FCSTD DOCUMENT  (FreeCAD 0.16R6703 (Git))
Label: icestick-case
License: All rights reserved
LicenseURL: http://en.wikipedia.org/wiki/All_rights_reserved
objects: Part::Feature×17, Part::Extrusion×17, Sketcher::SketchObject×10, Part::FeaturePython×10, Part::MultiFuse×7, PartDesign::Pocket×6, Part::Mirroring×6, App::DocumentObjectGroup×6, PartDesign::Pad×4, Part::Cut×2, Part::Part2DObjectPython×1
note: 90 computed .brp shape members not serialized (recipe doc carries the construction recipe); baked Part::Feature solids carry a one-line shape summary decoded from their .brp

FEATURE [Sketcher::SketchObject] Sketch001
  sketch-geometry (12):
    g0: LineSegment StartX=-53 StartY=-13.5 StartZ=0 EndX=-53 EndY=13.5 EndZ=0
    g1: LineSegment StartX=-49 StartY=-17.5 StartZ=0 EndX=49 EndY=-17.5 EndZ=0
    g2: LineSegment StartX=53 StartY=-13.5 StartZ=0 EndX=53 EndY=13.5 EndZ=0
    g3: LineSegment StartX=49 StartY=17.5 StartZ=0 EndX=-49 EndY=17.5 EndZ=0
    g4: ArcOfCircle CenterX=49 CenterY=-13.5 CenterZ=0 NormalX=0 NormalY=0 NormalZ=1 Radius=4 StartAngle=4.71239 EndAngle=6.28319
    g5: ArcOfCircle CenterX=49 CenterY=13.5 CenterZ=0 NormalX=0 NormalY=0 NormalZ=1 Radius=4 StartAngle=0 EndAngle=1.5708
    g6: ArcOfCircle CenterX=-49 CenterY=13.5 CenterZ=0 NormalX=0 NormalY=0 NormalZ=1 Radius=4 StartAngle=1.5708 EndAngle=3.14159
    g7: ArcOfCircle CenterX=-49 CenterY=-13.5 CenterZ=0 NormalX=0 NormalY=0 NormalZ=1 Radius=4 StartAngle=3.14159 EndAngle=4.71239
    g8: LineSegment [constr] StartX=-49 StartY=13.5 StartZ=0 EndX=49 EndY=13.5 EndZ=0
    g9: LineSegment [constr] StartX=49 StartY=13.5 StartZ=0 EndX=49 EndY=-13.5 EndZ=0
    g10: LineSegment [constr] StartX=49 StartY=-13.5 StartZ=0 EndX=-49 EndY=-13.5 EndZ=0
    g11: LineSegment [constr] StartX=-49 StartY=-13.5 StartZ=0 EndX=-49 EndY=13.5 EndZ=0
  constraints (30):
    c: Vertical(g0)
    c: Horizontal(g1)
    c: Vertical(g2)
    c: Horizontal(g3)
    c: Tangent(g1,g4) = -1.5708
    c: Tangent(g2,g4) = -1.5708
    c: Tangent(g2,g5) = -1.5708
    c: Tangent(g3,g5) = -1.5708
    c: Tangent(g0,g6) = 1.5708
    c: Tangent(g3,g6) = -1.5708
    c: Tangent(g1,g7) = -1.5708
    c: Equal(g7,g6)
    c: Equal(g6,g5)
    c: Symmetric(g4,g5,g-1)
    c: Radius(g4) = 4
    c: Coincident(g0,g7)
    c: Symmetric(g0,g2,g-2)
    c: Coincident(g8,g9)
    c: Coincident(g9,g10)
    c: Coincident(g10,g11)
    c: Coincident(g11,g8)
    c: Horizontal(g8)
    c: Horizontal(g10)
    c: Vertical(g9)
    c: Vertical(g11)
    c: Coincident(g8,g6)
    c: Coincident(g8,g5)
    c: Coincident(g10,g7)
    c: DistanceX(g10) = -98
    c: DistanceY(g9) = -27
FEATURE [PartDesign::Pad] Pad  label="Base"
  Length = 8
  Length2 = 100
  Sketch = -> Sketch001
  Type = 0
FEATURE [Sketcher::SketchObject] Sketch
  Placement = pos=(0,0,8) rot=(0,0,1;0rad)
  Support = -> Pad [Face10]
  sketch-geometry (16):
    g0: LineSegment [constr] StartX=-49 StartY=13.5 StartZ=0 EndX=49 EndY=13.5 EndZ=0
    g1: LineSegment [constr] StartX=49 StartY=13.5 StartZ=0 EndX=49 EndY=-13.5 EndZ=0
    g2: LineSegment [constr] StartX=49 StartY=-13.5 StartZ=0 EndX=-49 EndY=-13.5 EndZ=0
    g3: LineSegment [constr] StartX=-49 StartY=-13.5 StartZ=0 EndX=-49 EndY=13.5 EndZ=0
    g4: LineSegment StartX=-49 StartY=15.5 StartZ=0 EndX=49 EndY=15.5 EndZ=0
    g5: LineSegment StartX=51 StartY=13.5 StartZ=0 EndX=51 EndY=-13.5 EndZ=0
    g6: LineSegment StartX=49 StartY=-15.5 StartZ=0 EndX=-49 EndY=-15.5 EndZ=0
    g7: LineSegment StartX=-51 StartY=-13.5 StartZ=0 EndX=-51 EndY=13.5 EndZ=0
    g8: ArcOfCircle CenterX=-49 CenterY=13.5 CenterZ=0 NormalX=0 NormalY=0 NormalZ=1 Radius=2 StartAngle=1.5708 EndAngle=3.14159
    g9: ArcOfCircle CenterX=49 CenterY=13.5 CenterZ=0 NormalX=0 NormalY=0 NormalZ=1 Radius=2 StartAngle=0 EndAngle=1.5708
    g10: ArcOfCircle CenterX=-49 CenterY=-13.5 CenterZ=0 NormalX=0 NormalY=0 NormalZ=1 Radius=2 StartAngle=3.14159 EndAngle=4.71239
    g11: ArcOfCircle CenterX=49 CenterY=-13.5 CenterZ=0 NormalX=0 NormalY=0 NormalZ=1 Radius=2 StartAngle=4.71239 EndAngle=6.28319
    g12: LineSegment StartX=-57 StartY=21.5 StartZ=0 EndX=57 EndY=21.5 EndZ=0
    g13: LineSegment StartX=57 StartY=21.5 StartZ=0 EndX=57 EndY=-21.5 EndZ=0
    g14: LineSegment StartX=57 StartY=-21.5 StartZ=0 EndX=-57 EndY=-21.5 EndZ=0
    g15: LineSegment StartX=-57 StartY=-21.5 StartZ=0 EndX=-57 EndY=21.5 EndZ=0
  constraints (39):
    c: Coincident(g0,g1)
    c: Coincident(g1,g2)
    c: Coincident(g2,g3)
    c: Coincident(g3,g0)
    c: Horizontal(g2)
    c: Vertical(g3)
    c: DistanceX(g0) = 98
    c: DistanceY(g1) = -27
    c: Symmetric(g0,g0,g-2)
    c: Symmetric(g0,g1,g-1)
    c: Horizontal(g4)
    c: Horizontal(g6)
    c: Vertical(g5)
    c: Vertical(g7)
    c: Tangent(g4,g8) = 1.5708
    c: Tangent(g7,g8) = 1.5708
    c: Tangent(g4,g9) = 1.5708
    c: Tangent(g5,g9) = 1.5708
    c: Coincident(g8,g0)
    c: Radius(g8) = 2
    c: Coincident(g9,g0)
    c: Tangent(g6,g10) = 1.5708
    c: Tangent(g7,g10) = 1.5708
    c: Coincident(g10,g2)
    c: Tangent(g5,g11) = 1.5708
    c: Tangent(g6,g11) = 1.5708
    c: Coincident(g1,g11)
    c: Coincident(g12,g13)
    c: Coincident(g13,g14)
    c: Coincident(g14,g15)
    c: Coincident(g15,g12)
    c: Horizontal(g12)
    c: Horizontal(g14)
    c: Vertical(g13)
    c: Vertical(g15)
    c: Symmetric(g12,g12,g-2)
    c: Symmetric(g12,g14,g-1)
    c: DistanceY(g4,g12) = 6
    c: DistanceX(g5,g12) = 6
FEATURE [PartDesign::Pocket] Pocket
  Length = 7
  Sketch = -> Sketch
  Type = 0
FEATURE [Sketcher::SketchObject] Sketch002
  ExternalGeometry = -> [Pocket]
  Placement = pos=(0,0,8) rot=(0,0,1;0rad)
  Support = -> Pocket [Face19]
  sketch-geometry (17):
    g0: LineSegment StartX=-34.6 StartY=13.5 StartZ=0 EndX=48 EndY=13.5 EndZ=0
    g1: LineSegment StartX=48 StartY=13.5 StartZ=0 EndX=48 EndY=-13.5 EndZ=0
    g2: LineSegment StartX=-44 StartY=-8.95 StartZ=0 EndX=-34.6 EndY=-13.5 EndZ=0
    g3: LineSegment StartX=-34.6 StartY=-13.5 StartZ=0 EndX=48 EndY=-13.5 EndZ=0
    g4: LineSegment StartX=-34.6 StartY=13.5 StartZ=0 EndX=-44 EndY=8.95 EndZ=0
    g5: LineSegment StartX=-44 StartY=8.95 StartZ=0 EndX=-44 EndY=6.45 EndZ=0
    g6: LineSegment StartX=-44 StartY=6.45 StartZ=0 EndX=-48 EndY=6.45 EndZ=0
    g7: LineSegment StartX=-48 StartY=6.45 StartZ=0 EndX=-48 EndY=8.95 EndZ=0
    g8: LineSegment StartX=-48 StartY=8.95 StartZ=0 EndX=-53 EndY=8.95 EndZ=0
    g9: LineSegment StartX=-53 StartY=-8.95 StartZ=0 EndX=-48 EndY=-8.95 EndZ=0
    g10: LineSegment StartX=-48 StartY=-8.95 StartZ=0 EndX=-48 EndY=-6.45 EndZ=0
    g11: LineSegment StartX=-48 StartY=-6.45 StartZ=0 EndX=-44 EndY=-6.45 EndZ=0
    g12: LineSegment StartX=-44 StartY=-6.45 StartZ=0 EndX=-44 EndY=-8.95 EndZ=0
    g13: LineSegment [constr] StartX=-53 StartY=-8.95 StartZ=0 EndX=-53 EndY=8.95 EndZ=0
    g14: LineSegment StartX=-53 StartY=8.95 StartZ=0 EndX=-58 EndY=8.95 EndZ=0
    g15: LineSegment StartX=-58 StartY=8.95 StartZ=0 EndX=-58 EndY=-8.95 EndZ=0
    g16: LineSegment StartX=-58 StartY=-8.95 StartZ=0 EndX=-53 EndY=-8.95 EndZ=0
  constraints (48):
    c: Horizontal(g0)
    c: Coincident(g0,g1)
    c: Vertical(g1)
    c: Coincident(g3,g2)
    c: Coincident(g3,g1)
    c: Horizontal(g3)
    c: Coincident(g0,g4)
    c: Coincident(g5,g4)
    c: Vertical(g5)
    c: Coincident(g5,g6)
    c: Horizontal(g6)
    c: Coincident(g6,g7)
    c: Vertical(g7)
    c: Coincident(g7,g8)
    c: Horizontal(g8)
    c: Horizontal(g9)
    c: Coincident(g9,g10)
    c: Vertical(g10)
    c: Coincident(g10,g11)
    c: Coincident(g11,g12)
    c: Coincident(g12,g2)
    c: Vertical(g12)
    c: Horizontal(g11)
    c: DistanceY(g0,g1) = -27
    c: DistanceX(g6) = -4
    c: DistanceX(g4,g0) = 9.4
    c: DistanceX(g8) = -5
    c: DistanceY(g5,g11) = -12.9
    c: DistanceY(g7) = 2.5
    c: PointOnObject(g4,g8)
    c: Symmetric(g0,g1,g-1)
    c: Symmetric(g4,g2,g-1)
    c: Symmetric(g11,g5,g-1)
    c: Symmetric(g9,g7,g-1)
    c: Symmetric(g2,g0,g-1)
    c: Symmetric(g9,g8,g-1)
    c: Coincident(g13,g9)
    c: Coincident(g13,g8)
    c: Coincident(g8,g14)
    c: Horizontal(g14)
    c: Coincident(g14,g15)
    c: Vertical(g15)
    c: Coincident(g15,g16)
    c: Coincident(g16,g9)
    c: Horizontal(g16)
    c: PointOnObject(g9,g-3)
    c: DistanceX(g2,g1) = 92
    c: DistanceX(g15,g9) = 5
FEATURE [PartDesign::Pocket] Pocket001  label="bottom-box"
  Length = 7
  Sketch = -> Sketch002
  Type = 0
FEATURE [Sketcher::SketchObject] Sketch003  label="top-base-sketch"
  sketch-geometry (12):
    g0: LineSegment StartX=-53 StartY=-13.5 StartZ=0 EndX=-53 EndY=13.5 EndZ=0
    g1: LineSegment StartX=-49 StartY=-17.5 StartZ=0 EndX=49 EndY=-17.5 EndZ=0
    g2: LineSegment StartX=53 StartY=-13.5 StartZ=0 EndX=53 EndY=13.5 EndZ=0
    g3: LineSegment StartX=49 StartY=17.5 StartZ=0 EndX=-49 EndY=17.5 EndZ=0
    g4: ArcOfCircle CenterX=49 CenterY=-13.5 CenterZ=0 NormalX=0 NormalY=0 NormalZ=1 Radius=4 StartAngle=4.71239 EndAngle=6.28319
    g5: ArcOfCircle CenterX=49 CenterY=13.5 CenterZ=0 NormalX=0 NormalY=0 NormalZ=1 Radius=4 StartAngle=0 EndAngle=1.5708
    g6: ArcOfCircle CenterX=-49 CenterY=13.5 CenterZ=0 NormalX=0 NormalY=0 NormalZ=1 Radius=4 StartAngle=1.5708 EndAngle=3.14159
    g7: ArcOfCircle CenterX=-49 CenterY=-13.5 CenterZ=0 NormalX=0 NormalY=0 NormalZ=1 Radius=4 StartAngle=3.14159 EndAngle=4.71239
    g8: LineSegment [constr] StartX=-49 StartY=13.5 StartZ=0 EndX=49 EndY=13.5 EndZ=0
    g9: LineSegment [constr] StartX=49 StartY=13.5 StartZ=0 EndX=49 EndY=-13.5 EndZ=0
    g10: LineSegment [constr] StartX=49 StartY=-13.5 StartZ=0 EndX=-49 EndY=-13.5 EndZ=0
    g11: LineSegment [constr] StartX=-49 StartY=-13.5 StartZ=0 EndX=-49 EndY=13.5 EndZ=0
  constraints (30):
    c: Vertical(g0)
    c: Horizontal(g1)
    c: Vertical(g2)
    c: Horizontal(g3)
    c: Tangent(g1,g4) = -1.5708
    c: Tangent(g2,g4) = -1.5708
    c: Tangent(g2,g5) = -1.5708
    c: Tangent(g3,g5) = -1.5708
    c: Tangent(g0,g6) = 1.5708
    c: Tangent(g3,g6) = -1.5708
    c: Tangent(g1,g7) = -1.5708
    c: Equal(g7,g6)
    c: Equal(g6,g5)
    c: Symmetric(g4,g5,g-1)
    c: Radius(g4) = 4
    c: Coincident(g0,g7)
    c: Symmetric(g0,g2,g-2)
    c: Coincident(g8,g9)
    c: Coincident(g9,g10)
    c: Coincident(g10,g11)
    c: Coincident(g11,g8)
    c: Horizontal(g8)
    c: Horizontal(g10)
    c: Vertical(g9)
    c: Vertical(g11)
    c: Coincident(g8,g6)
    c: Coincident(g8,g5)
    c: Coincident(g10,g7)
    c: DistanceX(g10) = -98
    c: DistanceY(g9) = -27
FEATURE [PartDesign::Pad] Pad001  label="top-base"
  Length = 8
  Length2 = 100
  Sketch = -> Sketch003
  Type = 0
FEATURE [Sketcher::SketchObject] Sketch004
  Placement = pos=(0,0,8) rot=(0,0,1;0rad)
  Support = -> Pad001 [Face10]
  sketch-geometry (12):
    g0: LineSegment [constr] StartX=-49 StartY=13.5 StartZ=0 EndX=49 EndY=13.5 EndZ=0
    g1: LineSegment [constr] StartX=49 StartY=13.5 StartZ=0 EndX=49 EndY=-13.5 EndZ=0
    g2: LineSegment [constr] StartX=49 StartY=-13.5 StartZ=0 EndX=-49 EndY=-13.5 EndZ=0
    g3: LineSegment [constr] StartX=-49 StartY=-13.5 StartZ=0 EndX=-49 EndY=13.5 EndZ=0
    g4: LineSegment StartX=-49 StartY=15.8 StartZ=0 EndX=49 EndY=15.8 EndZ=0
    g5: LineSegment StartX=51.3 StartY=13.5 StartZ=0 EndX=51.3 EndY=-13.5 EndZ=0
    g6: LineSegment StartX=49 StartY=-15.8 StartZ=0 EndX=-49 EndY=-15.8 EndZ=0
    g7: LineSegment StartX=-51.3 StartY=-13.5 StartZ=0 EndX=-51.3 EndY=13.5 EndZ=0
    g8: ArcOfCircle CenterX=-49 CenterY=13.5 CenterZ=0 NormalX=0 NormalY=0 NormalZ=1 Radius=2.3 StartAngle=1.5708 EndAngle=3.14159
    g9: ArcOfCircle CenterX=49 CenterY=13.5 CenterZ=0 NormalX=0 NormalY=0 NormalZ=1 Radius=2.3 StartAngle=0 EndAngle=1.5708
    g10: ArcOfCircle CenterX=-49 CenterY=-13.5 CenterZ=0 NormalX=0 NormalY=0 NormalZ=1 Radius=2.3 StartAngle=3.14159 EndAngle=4.71239
    g11: ArcOfCircle CenterX=49 CenterY=-13.5 CenterZ=0 NormalX=0 NormalY=0 NormalZ=1 Radius=2.3 StartAngle=4.71239 EndAngle=6.28319
  constraints (29):
    c: Coincident(g0,g1)
    c: Coincident(g1,g2)
    c: Coincident(g2,g3)
    c: Coincident(g3,g0)
    c: Horizontal(g0)
    c: Horizontal(g2)
    c: Vertical(g1)
    c: Vertical(g3)
    c: DistanceX(g2) = -98
    c: DistanceY(g1) = -27
    c: Symmetric(g0,g0,g-2)
    c: Symmetric(g0,g2,g-1)
    c: Horizontal(g4)
    c: Horizontal(g6)
    c: Vertical(g5)
    c: Tangent(g4,g8) = 1.5708
    c: Tangent(g7,g8) = 1.5708
    c: Tangent(g4,g9) = 1.5708
    c: Tangent(g5,g9) = 1.5708
    c: Coincident(g8,g0)
    c: Coincident(g9,g0)
    c: Radius(g8) = 2.3
    c: Tangent(g6,g10) = 1.5708
    c: Tangent(g7,g10) = 1.5708
    c: Tangent(g5,g11) = 1.5708
    c: Tangent(g6,g11) = 1.5708
    c: Coincident(g10,g2)
    c: Symmetric(g7,g7,g-1)
    c: Coincident(g11,g1)
FEATURE [PartDesign::Pocket] Pocket002
  Length = 7
  Sketch = -> Sketch004
  Type = 0
FEATURE [Sketcher::SketchObject] Sketch005
  Placement = pos=(0,0,8) rot=(0,0,1;0rad)
  Support = -> Pocket002 [Face5]
  sketch-geometry (4):
    g0: LineSegment StartX=-55 StartY=8.95 StartZ=0 EndX=-50 EndY=8.95 EndZ=0
    g1: LineSegment StartX=-50 StartY=8.95 StartZ=0 EndX=-50 EndY=-8.95 EndZ=0
    g2: LineSegment StartX=-50 StartY=-8.95 StartZ=0 EndX=-55 EndY=-8.95 EndZ=0
    g3: LineSegment StartX=-55 StartY=-8.95 StartZ=0 EndX=-55 EndY=8.95 EndZ=0
  constraints (12):
    c: Coincident(g0,g1)
    c: Coincident(g1,g2)
    c: Coincident(g2,g3)
    c: Coincident(g3,g0)
    c: Horizontal(g0)
    c: Horizontal(g2)
    c: Vertical(g1)
    c: Vertical(g3)
    c: Symmetric(g0,g2,g-1)
    c: DistanceY(g3) = 17.9
    c: DistanceX(g0) = 5
    c: DistanceX(g-1,g1) = -50
FEATURE [PartDesign::Pocket] Pocket003
  Length = 7
  Sketch = -> Sketch005
  Type = 0
FEATURE [Sketcher::SketchObject] Sketch006
  Placement = pos=(0,0,1) rot=(0,0,1;0rad)
  Support = -> Pocket003 [Face22]
  sketch-geometry (8):
    g0: LineSegment [constr] StartX=-48.25 StartY=13.5 StartZ=0 EndX=48.25 EndY=13.5 EndZ=0
    g1: LineSegment [constr] StartX=48.25 StartY=13.5 StartZ=0 EndX=48.25 EndY=-13.5 EndZ=0
    g2: LineSegment [constr] StartX=48.25 StartY=-13.5 StartZ=0 EndX=-48.25 EndY=-13.5 EndZ=0
    g3: LineSegment [constr] StartX=-48.25 StartY=-13.5 StartZ=0 EndX=-48.25 EndY=13.5 EndZ=0
    g4: LineSegment StartX=18.25 StartY=13.5 StartZ=0 EndX=48.25 EndY=13.5 EndZ=0
    g5: LineSegment StartX=48.25 StartY=13.5 StartZ=0 EndX=48.25 EndY=-13.5 EndZ=0
    g6: LineSegment StartX=48.25 StartY=-13.5 StartZ=0 EndX=18.25 EndY=-13.5 EndZ=0
    g7: LineSegment StartX=18.25 StartY=-13.5 StartZ=0 EndX=18.25 EndY=13.5 EndZ=0
  constraints (24):
    c: Coincident(g0,g1)
    c: Coincident(g1,g2)
    c: Coincident(g2,g3)
    c: Coincident(g3,g0)
    c: Horizontal(g0)
    c: Horizontal(g2)
    c: Vertical(g1)
    c: Vertical(g3)
    c: Symmetric(g0,g2,g-1)
    c: DistanceY(g3) = 27
    c: DistanceX(g2) = -96.5
    c: Symmetric(g0,g0,g-2)
    c: Coincident(g4,g5)
    c: Coincident(g5,g6)
    c: Coincident(g6,g7)
    c: Coincident(g7,g4)
    c: Horizontal(g4)
    c: Horizontal(g6)
    c: Vertical(g5)
    c: Vertical(g7)
    c: Symmetric(g4,g6,g-1)
    c: PointOnObject(g5,g1)
    c: DistanceX(g4) = 30
    c: PointOnObject(g4,g0)
FEATURE [PartDesign::Pocket] Pocket004  label="top-box"
  Length = 5
  Sketch = -> Sketch006
  Type = 1
FEATURE [Part::FeaturePython] Clone  label="Bottom-part-clone"  # Draft clone (typed FeaturePython)
  Objects = -> [Pocket001]
  Placement = pos=(0,-18.6182,0) rot=(0,0,1;0rad)
  Scale = (1,1,1)
FEATURE [Part::FeaturePython] Clone001  label="top-part-clone"  # Draft clone (typed FeaturePython)
  Objects = -> [Pocket004]
  Placement = pos=(0,28.4831,0) rot=(0,0,1;0rad)
  Scale = (1,1,1)
FEATURE [Part::FeaturePython] Clone002  label="Bottom-part-clone2"  # Draft clone (typed FeaturePython)
  Objects = -> [Pocket001]
  Placement = pos=(0,-77.1136,0) rot=(0,0,1;0rad)
  Scale = (1,1,1)
FEATURE [Part::FeaturePython] Clone003  label="Top-part-clone2"  # Draft clone (typed FeaturePython)
  Objects = -> [Pocket004]
  Placement = pos=(0,-77.1136,9) rot=(1,0,0;3.14159rad)
  Scale = (1,1,1)
FEATURE [Sketcher::SketchObject] Sketch007  label="M3_screw_holder"
  Placement = pos=(0,0.5,0) rot=(0,0,1;0rad)
  sketch-geometry (5):
    g0: LineSegment StartX=-49 StartY=17 StartZ=0 EndX=-49 EndY=20 EndZ=0
    g1: LineSegment StartX=-42 StartY=17 StartZ=0 EndX=-42 EndY=20 EndZ=0
    g2: LineSegment StartX=-49 StartY=17 StartZ=0 EndX=-42 EndY=17 EndZ=0
    g3: ArcOfCircle CenterX=-45.5 CenterY=20 CenterZ=0 NormalX=0 NormalY=0 NormalZ=1 Radius=3.5 StartAngle=6.28319 EndAngle=9.42478
    g4: Circle CenterX=-45.5 CenterY=20 CenterZ=0 NormalX=0 NormalY=0 NormalZ=1 Radius=1.6799
  constraints (9):
    c: Vertical(g0)
    c: Vertical(g1)
    c: Coincident(g2,g0)
    c: Coincident(g2,g1)
    c: Horizontal(g2)
    c: Coincident(g3,g0)
    c: Coincident(g1,g3)
    c: Coincident(g4,g3)
    c: DistanceX(g0,g1) = 7
FEATURE [PartDesign::Pad] Pad002  label="M3_screw_hole"
  Length = 1
  Length2 = 100
  Placement = pos=(0,0.5,0) rot=(0,0,1;0rad)
  Sketch = -> Sketch007
  Type = 0
FEATURE [Part::Mirroring] Part__Mirroring  label="M3_screw_hole (Mirror #1)"
  Base = (0,0,0)
  Normal = (0,1,0)
  Source = -> Pad002
FEATURE [Part::Mirroring] Part__Mirroring001  label="M3_screw_hole (Mirror #2)"
  Base = (0,0,0)
  Normal = (1,0,0)
  Source = -> Part__Mirroring
FEATURE [Part::Mirroring] Part__Mirroring002  label="M3_screw_holes"
  Base = (0,0,0)
  Normal = (0,1,0)
  Source = -> Part__Mirroring001
FEATURE [Part::Feature] path3502
  shape: bbox 1.715 x 2.767 x 2e-07 mm, 0 faces, 0 solids (baked)
FEATURE [Part::Feature] path3502001
  shape: bbox 1.706 x 2.765 x 2e-07 mm, 0 faces, 0 solids (baked)
FEATURE [Part::Feature] path3502002
  shape: bbox 1.701 x 2.764 x 2e-07 mm, 0 faces, 0 solids (baked)
FEATURE [Part::Feature] path3502004
  shape: bbox 2.155 x 2.674 x 2e-07 mm, 0 faces, 0 solids (baked)
FEATURE [Part::Feature] path3502005
  shape: bbox 0.4815 x 0.647 x 2e-07 mm, 0 faces, 0 solids (baked)
FEATURE [Part::Feature] path3502006
  shape: bbox 3.65 x 2.702 x 2e-07 mm, 0 faces, 0 solids (baked)
FEATURE [Part::Feature] path3502007
  shape: bbox 3.443 x 2.55 x 2e-07 mm, 0 faces, 0 solids (baked)
FEATURE [Part::Feature] path3502008
  shape: bbox 2.211 x 3.442 x 2e-07 mm, 0 faces, 0 solids (baked)
FEATURE [Part::Feature] path3502009
  shape: bbox 1.95 x 3.375 x 2e-07 mm, 0 faces, 0 solids (baked)
FEATURE [Part::Feature] path3502010
  shape: bbox 2.286 x 3.375 x 2e-07 mm, 0 faces, 0 solids (baked)
FEATURE [Part::Feature] path3502011
  shape: bbox 0.525 x 0.825 x 2e-07 mm, 0 faces, 0 solids (baked)
FEATURE [Part::Feature] path3502012
  shape: bbox 2.685 x 3.382 x 2e-07 mm, 0 faces, 0 solids (baked)
FEATURE [Part::Feature] path3502013
  shape: bbox 0.4025 x 1.088 x 2e-07 mm, 0 faces, 0 solids (baked)
FEATURE [Part::Feature] path3502014
  shape: bbox 1.713 x 2.7 x 2e-07 mm, 0 faces, 0 solids (baked)
FEATURE [Part::Feature] path3502015
  shape: bbox 1.7 x 2.694 x 2e-07 mm, 0 faces, 0 solids (baked)
FEATURE [Part::Feature] path3502016
  shape: bbox 1.714 x 2.674 x 2e-07 mm, 0 faces, 0 solids (baked)
FEATURE [Part::Extrusion] Extrude_path3502  label="path3502_Extrude"
  Base = -> path3502
  Dir = (0,0,5)
  Solid = true
FEATURE [Part::Extrusion] Extrude_path3502001  label="path3502001_Extrude"
  Base = -> path3502001
  Dir = (0,0,5)
  Solid = true
FEATURE [Part::Extrusion] Extrude_path3502002  label="path3502002_Extrude"
  Base = -> path3502002
  Dir = (0,0,5)
  Solid = true
FEATURE [Part::Extrusion] Extrude_path3502004  label="path3502004_Extrude"
  Base = -> path3502004
  Dir = (0,0,5)
  Solid = true
FEATURE [Part::Extrusion] Extrude_path3502006  label="path3502006_Extrude"
  Base = -> path3502006
  Dir = (0,0,5)
  Solid = true
FEATURE [Part::Extrusion] Extrude_path3502007  label="path3502007_Extrude"
  Base = -> path3502007
  Dir = (0,0,5)
  Solid = true
FEATURE [Part::Extrusion] Extrude_path3502008  label="path3502008_Extrude"
  Base = -> path3502008
  Dir = (0,0,5)
  Solid = true
FEATURE [Part::Extrusion] Extrude_path3502009  label="path3502009_Extrude"
  Base = -> path3502009
  Dir = (0,0,5)
  Solid = true
FEATURE [Part::Extrusion] Extrude_path3502010  label="path3502010_Extrude"
  Base = -> path3502010
  Dir = (0,0,5)
  Solid = true
FEATURE [Part::Extrusion] Extrude_path3502012  label="path3502012_Extrude"
  Base = -> path3502012
  Dir = (0,0,5)
  Solid = true
FEATURE [Part::Extrusion] Extrude_path3502014  label="path3502014_Extrude"
  Base = -> path3502014
  Dir = (0,0,5)
  Solid = true
FEATURE [Part::Extrusion] Extrude_path3502015  label="path3502015_Extrude"
  Base = -> path3502015
  Dir = (0,0,5)
  Solid = true
FEATURE [Part::Extrusion] Extrude_path3502016  label="path3502016_Extrude"
  Base = -> path3502016
  Dir = (0,0,5)
  Solid = true
FEATURE [Part::Extrusion] Extrude_path3502005  label="path3502005_Extrude"
  Base = -> path3502005
  Dir = (0,0,10)
  Solid = true
FEATURE [Part::Extrusion] Extrude_path3502011  label="path3502011_Extrude"
  Base = -> path3502011
  Dir = (0,0,10)
  Solid = true
FEATURE [Part::Extrusion] Extrude_path3502013  label="path3502013_Extrude"
  Base = -> path3502013
  Dir = (0,0,10)
  Solid = true
FEATURE [Part::MultiFuse] Fusion001
  Shapes = -> [Extrude_path3502004,Extrude_path3502006,Extrude_path3502007,Extrude_path3502008,Extrude_path3502009,Extrude_path3502010,Extrude_path3502012]
FEATURE [Part::MultiFuse] Fusion002
  Shapes = -> [Extrude_path3502013,Extrude_path3502011,Extrude_path3502005]
FEATURE [Part::Cut] Cut
  Base = -> Fusion001
  Tool = -> Fusion002
FEATURE [Part::MultiFuse] Fusion003
  Shapes = -> [Extrude_path3502,Extrude_path3502001,Extrude_path3502002]
FEATURE [Part::MultiFuse] Fusion004
  Shapes = -> [Extrude_path3502016,Extrude_path3502014,Extrude_path3502015]
FEATURE [Part::MultiFuse] Fusion005  label="fpga_wars_icon"
  Placement = pos=(8,20.6,0) rot=(1,0,0;3.14159rad)
  Shapes = -> [Cut,Fusion003,Fusion004]
FEATURE [Sketcher::SketchObject] Sketch023  label="M3_screw_holder001"
  Placement = pos=(0,0.5,0) rot=(0,0,1;0rad)
  sketch-geometry (5):
    g0: LineSegment StartX=-49 StartY=17 StartZ=0 EndX=-49 EndY=20 EndZ=0
    g1: LineSegment StartX=-42 StartY=17 StartZ=0 EndX=-42 EndY=20 EndZ=0
    g2: LineSegment StartX=-49 StartY=17 StartZ=0 EndX=-42 EndY=17 EndZ=0
    g3: ArcOfCircle CenterX=-45.5 CenterY=20 CenterZ=0 NormalX=0 NormalY=0 NormalZ=1 Radius=3.5 StartAngle=6.28319 EndAngle=9.42478
    g4: Circle CenterX=-45.5 CenterY=20 CenterZ=0 NormalX=0 NormalY=0 NormalZ=1 Radius=1.6799
  constraints (9):
    c: Vertical(g0)
    c: Vertical(g1)
    c: Coincident(g2,g0)
    c: Coincident(g2,g1)
    c: Horizontal(g2)
    c: Coincident(g3,g0)
    c: Coincident(g1,g3)
    c: Coincident(g4,g3)
    c: DistanceX(g0,g1) = 7
FEATURE [PartDesign::Pad] Pad009  label="M3_screw_hole001"
  Length = 1
  Length2 = 100
  Placement = pos=(0,0.5,0) rot=(0,0,1;0rad)
  Sketch = -> Sketch023
  Type = 0
FEATURE [Part::Mirroring] Part__Mirroring003  label="M3_screw_hole (Mirror #1)001"
  Base = (0,0,0)
  Normal = (0,1,0)
  Source = -> Pad009
FEATURE [Part::Mirroring] Part__Mirroring004  label="M3_screw_hole (Mirror #2)001"
  Base = (0,0,0)
  Normal = (1,0,0)
  Source = -> Part__Mirroring003
FEATURE [Part::Mirroring] Part__Mirroring005  label="M3_screw_holes001"
  Base = (0,0,0)
  Normal = (0,1,0)
  Source = -> Part__Mirroring004
FEATURE [Sketcher::SketchObject] Sketch025
  Placement = pos=(0,0,8) rot=(0,0,1;0rad)
  sketch-geometry (17):
    g0: LineSegment StartX=-34.6 StartY=13.5 StartZ=0 EndX=48 EndY=13.5 EndZ=0
    g1: LineSegment StartX=48 StartY=13.5 StartZ=0 EndX=48 EndY=-13.5 EndZ=0
    g2: LineSegment StartX=-44 StartY=-8.95 StartZ=0 EndX=-34.6 EndY=-13.5 EndZ=0
    g3: LineSegment StartX=-34.6 StartY=-13.5 StartZ=0 EndX=48 EndY=-13.5 EndZ=0
    g4: LineSegment StartX=-34.6 StartY=13.5 StartZ=0 EndX=-44 EndY=8.95 EndZ=0
    g5: LineSegment StartX=-44 StartY=8.95 StartZ=0 EndX=-44 EndY=6.45 EndZ=0
    g6: LineSegment StartX=-44 StartY=6.45 StartZ=0 EndX=-48 EndY=6.45 EndZ=0
    g7: LineSegment StartX=-48 StartY=6.45 StartZ=0 EndX=-48 EndY=8.95 EndZ=0
    g8: LineSegment StartX=-48 StartY=8.95 StartZ=0 EndX=-53 EndY=8.95 EndZ=0
    g9: LineSegment StartX=-53 StartY=-8.95 StartZ=0 EndX=-48 EndY=-8.95 EndZ=0
    g10: LineSegment StartX=-48 StartY=-8.95 StartZ=0 EndX=-48 EndY=-6.45 EndZ=0
    g11: LineSegment StartX=-48 StartY=-6.45 StartZ=0 EndX=-44 EndY=-6.45 EndZ=0
    g12: LineSegment StartX=-44 StartY=-6.45 StartZ=0 EndX=-44 EndY=-8.95 EndZ=0
    g13: LineSegment [constr] StartX=-53 StartY=-8.95 StartZ=0 EndX=-53 EndY=8.95 EndZ=0
    g14: LineSegment StartX=-53 StartY=8.95 StartZ=0 EndX=-58 EndY=8.95 EndZ=0
    g15: LineSegment StartX=-58 StartY=8.95 StartZ=0 EndX=-58 EndY=-8.95 EndZ=0
    g16: LineSegment StartX=-58 StartY=-8.95 StartZ=0 EndX=-53 EndY=-8.95 EndZ=0
  constraints (47):
    c: Horizontal(g0)
    c: Coincident(g0,g1)
    c: Vertical(g1)
    c: Coincident(g3,g2)
    c: Coincident(g3,g1)
    c: Horizontal(g3)
    c: Coincident(g0,g4)
    c: Coincident(g5,g4)
    c: Vertical(g5)
    c: Coincident(g5,g6)
    c: Horizontal(g6)
    c: Coincident(g6,g7)
    c: Vertical(g7)
    c: Coincident(g7,g8)
    c: Horizontal(g8)
    c: Horizontal(g9)
    c: Coincident(g9,g10)
    c: Vertical(g10)
    c: Coincident(g10,g11)
    c: Coincident(g11,g12)
    c: Coincident(g12,g2)
    c: Vertical(g12)
    c: Horizontal(g11)
    c: DistanceY(g0,g1) = -27
    c: DistanceX(g6) = -4
    c: DistanceX(g4,g0) = 9.4
    c: DistanceX(g8) = -5
    c: DistanceY(g5,g11) = -12.9
    c: DistanceY(g7) = 2.5
    c: PointOnObject(g4,g8)
    c: Symmetric(g0,g1,g-1)
    c: Symmetric(g4,g2,g-1)
    c: Symmetric(g11,g5,g-1)
    c: Symmetric(g9,g7,g-1)
    c: Symmetric(g2,g0,g-1)
    c: Symmetric(g9,g8,g-1)
    c: Coincident(g13,g9)
    c: Coincident(g13,g8)
    c: Coincident(g8,g14)
    c: Horizontal(g14)
    c: Coincident(g14,g15)
    c: Vertical(g15)
    c: Coincident(g15,g16)
    c: Coincident(g16,g9)
    c: Horizontal(g16)
    c: DistanceX(g2,g1) = 92
    c: DistanceX(g15,g9) = 5
FEATURE [PartDesign::Pocket] Pocket013  label="bottom-box001"
  Length = 7
  Sketch = -> Sketch025
  Type = 0
FEATURE [Part::MultiFuse] Fusion  label="bottom-box-holes-screws"
  Shapes = -> [Pocket013,Part__Mirroring005,Part__Mirroring004,Part__Mirroring003,Pad009]
FEATURE [App::DocumentObjectGroup] Group001  label="Bottom-part"
  Group = -> [Pad,Pocket,Pocket001,Part__Mirroring002,Fusion]
FEATURE [Part::FeaturePython] Clone007004  label="Clone of top-box"  # Draft clone (typed FeaturePython)
  Objects = -> [Pocket004]
  Placement = pos=(0,0,9) rot=(1,0,0;3.14159rad)
  Scale = (1,1,1)
FEATURE [Part::Feature] Clone007005  label="fpga_wars_icon-clone002"
  Placement = pos=(8,-0.6,8.5) rot=(0,0,1;0rad)
  shape: bbox 9.65 x 14.24 x 5 mm, 1646 faces, 13 solids (baked)
FEATURE [Part::Part2DObjectPython] ShapeString  # Draft 2D object (typed FeaturePython)
  FontFile = <path>
  Placement = pos=(-38.4879,4.45392,0) rot=(0,0,1;0rad)
  Size = 10
  String = ICEstick
  Tracking = 0
FEATURE [Part::Extrusion] Extrude_ShapeString  label="icestick_text"
  Base = -> ShapeString
  Dir = (0,0,5)
  Solid = true
FEATURE [Part::FeaturePython] Clone007008  label="ICEstick_text"  # WARN: FeaturePython — macro-defined, semantics opaque (R4)
  Placement = pos=(-9,-7.5,8.5) rot=(0,0,1;0rad)
  Scale = (1,1,1)
FEATURE [Part::MultiFuse] Fusion007  label="logo_and_text"
  Shapes = -> [Clone007005,Clone007008]
FEATURE [Part::Cut] Cut002  label="Top-box_text_and_logo"
  Base = -> Clone007004
  Tool = -> Fusion007
FEATURE [App::DocumentObjectGroup] Group002  label="Top-part"
  Group = -> [Pad001,Pocket002,Pocket003,Pocket004,Cut002]
FEATURE [App::DocumentObjectGroup] Grupo  label="text_and_logos"
  Group = -> [Fusion005,Extrude_ShapeString]
FEATURE [App::DocumentObjectGroup] Group  label="src"
  Group = -> [Group001,Group002,Grupo]
FEATURE [Part::FeaturePython] Clone007009  label="Top-box_text_and_logo001"  # Draft clone (typed FeaturePython)
  Objects = -> [Cut002]
  Placement = pos=(0,-23,0) rot=(0,0,1;0rad)
  Scale = (1,1,1)
FEATURE [Part::FeaturePython] Clone007010  label="bottom-box-holes-screws-clone"  # WARN: FeaturePython — macro-defined, semantics opaque (R4)
  Placement = pos=(0,-19,0) rot=(0,0,1;0rad)
  Scale = (1,1,1)
FEATURE [Part::FeaturePython] Clone007011  label="bottom-box-holes-screws-clone001"  # WARN: FeaturePython — macro-defined, semantics opaque (R4)
  Placement = pos=(0,-23,0) rot=(0,0,1;0rad)
  Scale = (1,1,1)
FEATURE [App::DocumentObjectGroup] Group004  label="Assembly"
  Group = -> [Clone002,Clone003,Clone007009,Clone007011]
FEATURE [Part::FeaturePython] Clone007015  label="Top-box_text_and_logo003"  # WARN: FeaturePython — macro-defined, semantics opaque (R4)
  Placement = pos=(0,28.5,9) rot=(1,0,0;3.14159rad)
  Scale = (1,1,1)
FEATURE [App::DocumentObjectGroup] Group003  label="printing-plate"
  Group = -> [Clone,Clone001,Clone007010,Clone007015]
note: 1 file-system path scrubbed to <path> (originals preserved in the JSON sidecar)
